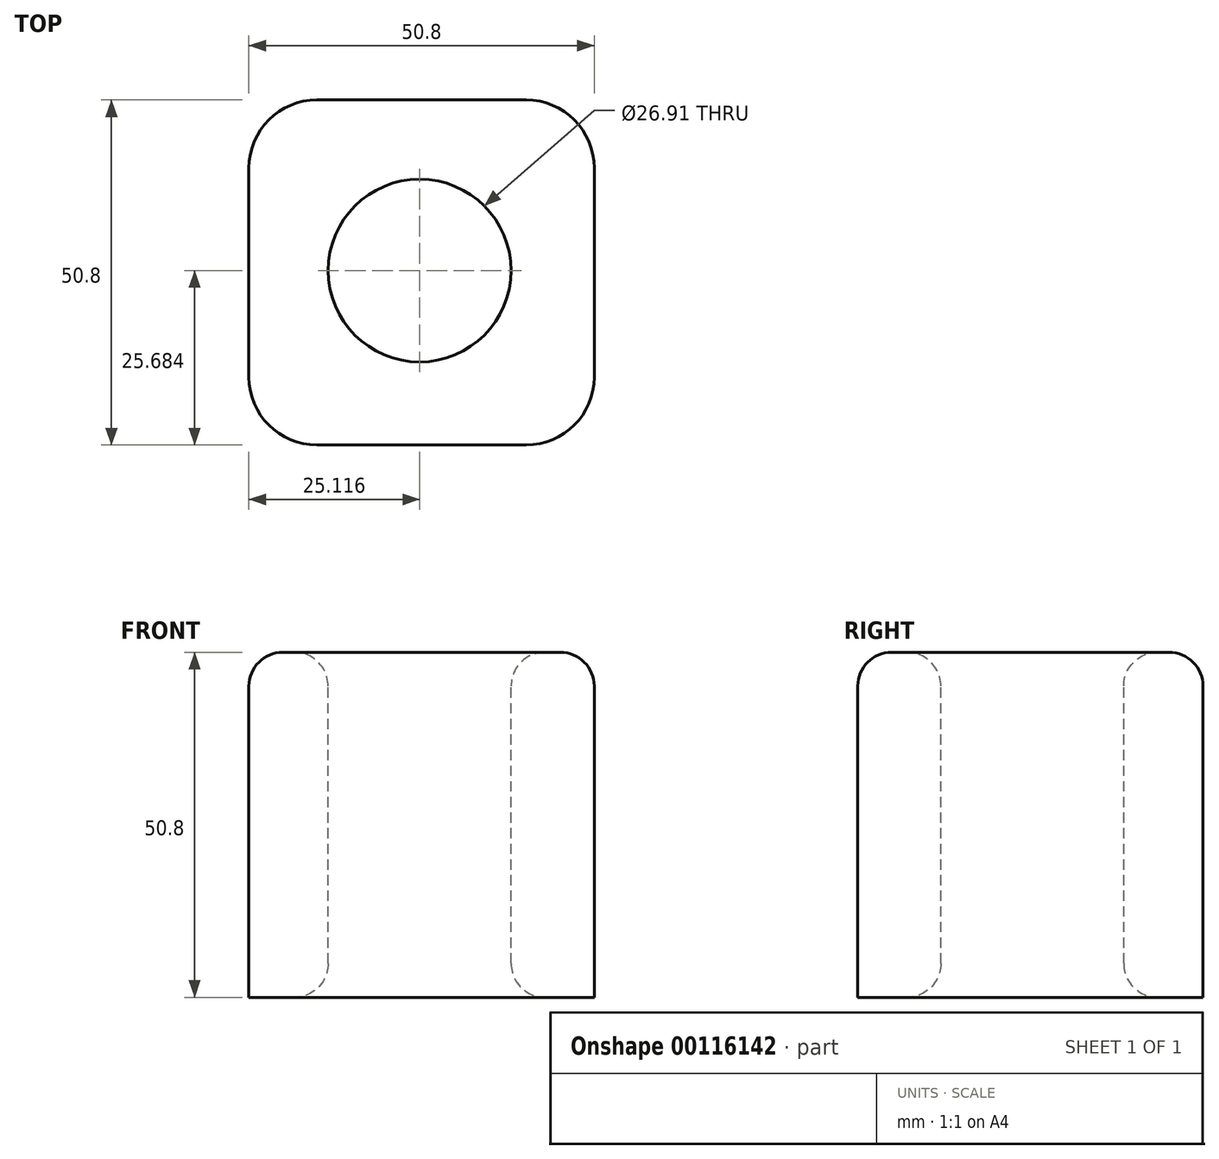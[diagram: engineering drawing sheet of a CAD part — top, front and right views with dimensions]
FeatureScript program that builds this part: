
annotation { "Feature Type Name" : "Feature", "Feature Type Description" : "" }
export const myFeature = defineFeature(function(context is Context, id is Id, definition is map)
    precondition{}
    {
        {
            var Q0;
            Q0=qCreatedBy(makeId("Top.planeOp"),FACE);
            var sketch = newSketch(context, id + "F0", { "sketchPlane" : qUnion([Q0])});
            skLineSegment(sketch, "E0.bottom", {"start": v(0, 0) * mm, "end": v(50.8, 0) * mm});
            skLineSegment(sketch, "E0.top", {"start": v(0, 50.8) * mm, "end": v(50.8, 50.8) * mm});
            skLineSegment(sketch, "E0.left", {"start": v(0, 0) * mm, "end": v(0, 50.8) * mm});
            skLineSegment(sketch, "E0.right", {"start": v(50.8, 0) * mm, "end": v(50.8, 50.8) * mm});
            skSolve(sketch);
        }
        {
            var Q0;
            Q0=makeQuery(id+"F0.imprint","IMPRINT",FACE,{"disambiguationData":[TD([[makeQuery(id+"F0.imprint","IMPRINT",EDGE,{"derivedFrom":sQuery(id+"F0.wireOp",EDGE,"E0.bottom")}),1.0]])]});
            extrude(context, id + "F1", {"entities" : qUnion([Q0]), "depth" : 50.8 * mm});
        }
        {
            var Q0;
            Q0=makeQuery(id+"F1.opExtrude","CAP_FACE",FACE,{"disambiguationData":[OSD([sQuery(id+"F0.wireOp",EDGE,"E0.bottom"),sQuery(id+"F0.wireOp",EDGE,"E0.top"),sQuery(id+"F0.wireOp",EDGE,"E0.left"),sQuery(id+"F0.wireOp",EDGE,"E0.right")])],"isStart":false});
            var sketch = newSketch(context, id + "F2", { "sketchPlane" : qUnion([Q0])});
            skPoint(sketch, "E1", {"position": v(0, 25.4) * mm});
            skPoint(sketch, "E2", {"position": v(25.4, 0) * mm});
            skPoint(sketch, "E3", {"position": v(50.8, 25.4) * mm});
            skPoint(sketch, "E4", {"position": v(25.4, 50.8) * mm});
            skCircle(sketch, "E5", {"center": v(25.12, 25.68) * mm, "radius": 13.45 * mm});
            skSolve(sketch);
        }
        {
            var Q0;
            Q0=makeQuery(id+"F2.imprint","IMPRINT",FACE,{"disambiguationData":[TD([[makeQuery(id+"F2.imprint","IMPRINT",EDGE,{"derivedFrom":sQuery(id+"F2.wireOp",EDGE,"E5")}),1.0]])]});
            extrude(context, id + "F3", {"entities" : qUnion([Q0]), "operationType" : NewBodyOperationType.REMOVE, "endBound" : BoundingType.THROUGH_ALL, "oppositeDirection" : true, "depth" : 25 * mm});
        }
        {
            var Q0;
            Q0=makeQuery(id+"F1.opExtrude","SWEPT_EDGE",EDGE,{"disambiguationData":[OSD([sQuery(id+"F0.wireOp",EDGE,"E0.top"),sQuery(id+"F0.wireOp",EDGE,"E0.right")])]});
            var Q1;
            Q1=makeQuery(id+"F1.opExtrude","SWEPT_EDGE",EDGE,{"disambiguationData":[OSD([sQuery(id+"F0.wireOp",EDGE,"E0.bottom"),sQuery(id+"F0.wireOp",EDGE,"E0.right")])]});
            var Q2;
            Q2=makeQuery(id+"F1.opExtrude","SWEPT_EDGE",EDGE,{"disambiguationData":[OSD([sQuery(id+"F0.wireOp",EDGE,"E0.top"),sQuery(id+"F0.wireOp",EDGE,"E0.left")])]});
            var Q3;
            Q3=makeQuery(id+"F1.opExtrude","SWEPT_EDGE",EDGE,{"disambiguationData":[OSD([sQuery(id+"F0.wireOp",EDGE,"E0.bottom"),sQuery(id+"F0.wireOp",EDGE,"E0.left")])]});
            fillet(context, id + "F4", {"entities" : qUnion([Q0, Q1, Q2, Q3]), "radius" : 10 * mm, "tangentPropagation" : true, "allowEdgeOverflow" : false});
        }
        {
            var Q0;
            Q0=makeQuery(id+"F3.boolean.opBoolean","COPY",EDGE,{"derivedFrom":makeQuery(id+"F3.opExtrude","CAP_EDGE",EDGE,{"disambiguationData":[OSD([sQuery(id+"F2.wireOp",EDGE,"E5")])],"isStart":true})});
            var Q1;
            Q1=makeQuery(id+"F3.boolean.opBoolean","INTERSECT",EDGE,{"derivedFrom":[makeQuery(id+"F1.opExtrude","CAP_FACE",FACE,{"disambiguationData":[OSD([sQuery(id+"F0.wireOp",EDGE,"E0.bottom"),sQuery(id+"F0.wireOp",EDGE,"E0.top"),sQuery(id+"F0.wireOp",EDGE,"E0.left"),sQuery(id+"F0.wireOp",EDGE,"E0.right")])],"isStart":true}),makeQuery(id+"F3.opExtrude","SWEPT_FACE",FACE,{"disambiguationData":[OSD([sQuery(id+"F2.wireOp",EDGE,"E5")])]})]});
            var Q2;
            Q2=makeQuery(id+"F1.opExtrude","CAP_FACE",FACE,{"disambiguationData":[OSD([sQuery(id+"F0.wireOp",EDGE,"E0.bottom"),sQuery(id+"F0.wireOp",EDGE,"E0.top"),sQuery(id+"F0.wireOp",EDGE,"E0.left"),sQuery(id+"F0.wireOp",EDGE,"E0.right")])],"isStart":false});
            fillet(context, id + "F5", {"entities" : qUnion([Q0, Q1, Q2]), "radius" : 5 * mm, "tangentPropagation" : true, "allowEdgeOverflow" : false});
        }
    });
